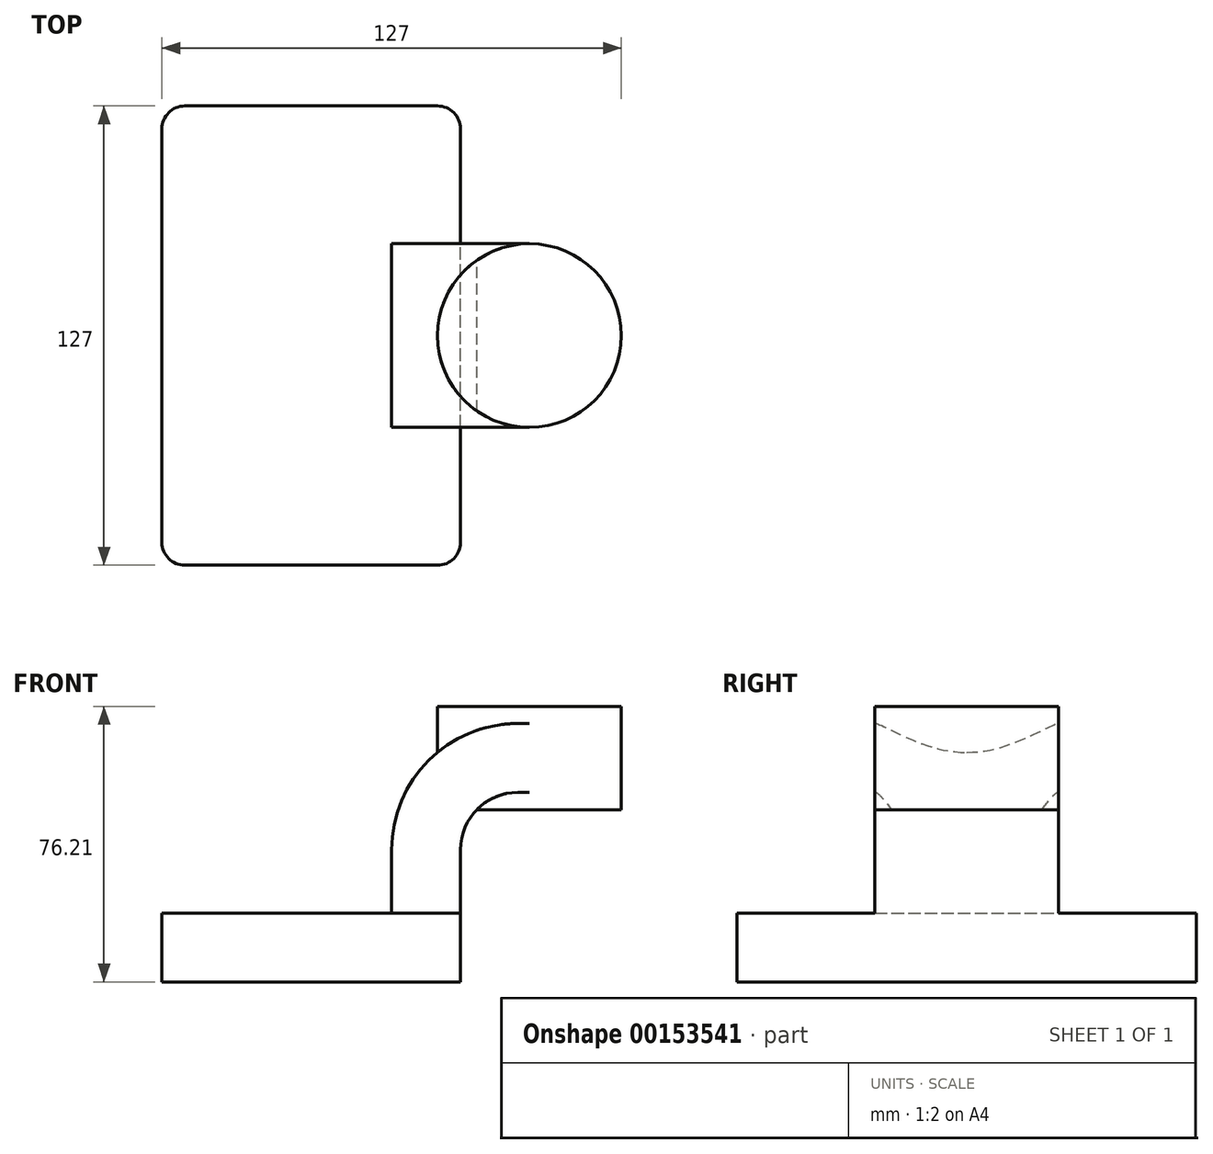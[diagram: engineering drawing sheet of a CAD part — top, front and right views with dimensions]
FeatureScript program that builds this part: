
annotation { "Feature Type Name" : "Feature", "Feature Type Description" : "" }
export const myFeature = defineFeature(function(context is Context, id is Id, definition is map)
    precondition{}
    {
        {
            var Q0;
            Q0=qCreatedBy(makeId("Front.planeOp"),FACE);
            var sketch = newSketch(context, id + "F0", { "sketchPlane" : qUnion([Q0])});
            skLineSegment(sketch, "E0.bottom", {"start": v(41.28, -9.52) * mm, "end": v(-41.27, -9.53) * mm});
            skLineSegment(sketch, "E0.top", {"start": v(41.27, 9.53) * mm, "end": v(-41.28, 9.53) * mm});
            skLineSegment(sketch, "E0.left", {"start": v(41.28, -9.52) * mm, "end": v(41.28, 9.53) * mm});
            skLineSegment(sketch, "E0.right", {"start": v(-41.27, -9.53) * mm, "end": v(-41.28, 9.53) * mm});
            skPoint(sketch, "E0.middle", {"position": v(0, 0) * mm});
            skLineSegment(sketch, "E1.bottom", {"start": v(111.12, 38.1) * mm, "end": v(60.33, 38.1) * mm});
            skLineSegment(sketch, "E1.top", {"start": v(111.12, 66.68) * mm, "end": v(60.33, 66.68) * mm});
            skLineSegment(sketch, "E1.left", {"start": v(111.12, 38.1) * mm, "end": v(111.12, 66.68) * mm});
            skLineSegment(sketch, "E1.right", {"start": v(60.33, 38.1) * mm, "end": v(60.33, 66.68) * mm});
            skPoint(sketch, "E1.middle", {"position": v(85.72, 52.39) * mm});
            skLineSegment(sketch, "E2", {"start": v(41.27, 9.53) * mm, "end": v(41.27, 27) * mm});
            skArc(sketch, "E3", {"start": v(41.27, 27) * mm, "mid": v(45.92, 38.23) * mm, "end": v(57.15, 42.88) * mm});
            skLineSegment(sketch, "E4", {"start": v(57.15, 42.88) * mm, "end": v(85.75, 42.88) * mm});
            skLineSegment(sketch, "E5.0", {"start": v(57.15, 61.93) * mm, "end": v(85.75, 61.93) * mm});
            skArc(sketch, "E5.1", {"start": v(22.23, 27) * mm, "mid": v(32.45, 51.7) * mm, "end": v(57.15, 61.93) * mm});
            skLineSegment(sketch, "E5.2", {"start": v(22.23, 9.53) * mm, "end": v(22.23, 27) * mm});
            skLineSegment(sketch, "E6", {"start": v(85.72, 38.1) * mm, "end": v(85.72, 66.68) * mm});
            skFitSpline(sketch, "E7", {"points": [v(-41.28, 9.53) * mm, v(57.15, 61.93) * mm], "startDerivative": vector(40.93, 87.18) * mm, "endDerivative": vector(191, -1.05) * mm});
            skSolve(sketch);
        }
        {
            var Q0;
            Q0=makeQuery(id+"F0.imprint","IMPRINT",FACE,{"disambiguationData":[TD([[makeQuery(id+"F0.imprint","IMPRINT",EDGE,{"derivedFrom":sQuery(id+"F0.wireOp",EDGE,"E0.bottom")}),-1.0]])]});
            extrude(context, id + "F1", {"entities" : qUnion([Q0]), "endBound" : BoundingType.SYMMETRIC, "depth" : 127 * mm});
        }
        {
            var Q0;
            {var subQ1=sQuery(id+"F0.wireOp",EDGE,"E2");Q0=makeQuery(id+"F0.imprint","IMPRINT",FACE,{"disambiguationData":[TD([[makeQuery(id+"F0.imprint","IMPRINT",EDGE,{"derivedFrom":subQ1}),1.0]])]});}
            extrude(context, id + "F2", {"entities" : qUnion([Q0]), "operationType" : NewBodyOperationType.ADD, "endBound" : BoundingType.SYMMETRIC, "depth" : 50.8 * mm});
        }
        {
            var Q0;
            Q0=makeQuery(id+"F0.imprint","IMPRINT",FACE,{"disambiguationData":[TD([[makeQuery(id+"F0.imprint","IMPRINT",EDGE,{"derivedFrom":sQuery(id+"F0.wireOp",EDGE,"E5.1")}),1.0]])]});
            extrude(context, id + "F3", {"entities" : qUnion([Q0]), "operationType" : NewBodyOperationType.ADD, "endBound" : BoundingType.SYMMETRIC, "depth" : 15.88 * mm});
        }
        {
            var Q0;
            {var subQ0=sQuery(id+"F0.wireOp",EDGE,"E1.right");var subQ1=sQuery(id+"F0.wireOp",EDGE,"E1.top");var subQ2=makeQuery(id+"F0.imprint","INTERSECT",VERTEX,{"derivedFrom":[subQ1,subQ0]});Q0=makeQuery(id+"F0.imprint","IMPRINT",FACE,{"disambiguationData":[TD([[makeQuery(id+"F0.imprint","IMPRINT",EDGE,{"disambiguationData":[TD([[subQ2,1.0]])],"derivedFrom":subQ1}),1.0]])]});}
            var Q1;
            {var subQ0=sQuery(id+"F0.wireOp",EDGE,"E1.right");var subQ1=sQuery(id+"F0.wireOp",EDGE,"E1.bottom");var subQ2=makeQuery(id+"F0.imprint","INTERSECT",VERTEX,{"derivedFrom":[subQ1,subQ0]});Q1=makeQuery(id+"F0.imprint","IMPRINT",FACE,{"disambiguationData":[TD([[makeQuery(id+"F0.imprint","IMPRINT",EDGE,{"disambiguationData":[TD([[subQ2,1.0]])],"derivedFrom":subQ1}),-1.0]])]});}
            var Q2;
            {var subQ0=sQuery(id+"F0.wireOp",EDGE,"E4");var subQ1=sQuery(id+"F0.wireOp",EDGE,"E1.right");var subQ2=makeQuery(id+"F0.imprint","INTERSECT",VERTEX,{"derivedFrom":[subQ1,subQ0]});Q2=makeQuery(id+"F0.imprint","IMPRINT",FACE,{"disambiguationData":[TD([[makeQuery(id+"F0.imprint","IMPRINT",EDGE,{"disambiguationData":[TD([[subQ2,-1.0]])],"derivedFrom":subQ1}),-1.0]])]});}
            var Q3;
            Q3=sQuery(id+"F0.wireOp",EDGE,"E1.right");
            revolve(context, id + "F4", {"operationType" : NewBodyOperationType.ADD, "entities" : qUnion([Q0, Q1, Q2]), "axis" : qUnion([Q3]), "revolveType" : RevolveType.FULL});
        }
        {
            var Q0;
            Q0=makeQuery(id+"F1.opExtrude","CAP_EDGE",EDGE,{"disambiguationData":[OSD([sQuery(id+"F0.wireOp",EDGE,"E0.left")])],"isStart":false});
            var Q1;
            Q1=makeQuery(id+"F1.opExtrude","CAP_EDGE",EDGE,{"disambiguationData":[OSD([sQuery(id+"F0.wireOp",EDGE,"E0.right")])],"isStart":false});
            var Q2;
            Q2=makeQuery(id+"F1.opExtrude","CAP_EDGE",EDGE,{"disambiguationData":[OSD([sQuery(id+"F0.wireOp",EDGE,"E0.left")])],"isStart":true});
            var Q3;
            Q3=makeQuery(id+"F1.opExtrude","CAP_EDGE",EDGE,{"disambiguationData":[OSD([sQuery(id+"F0.wireOp",EDGE,"E0.right")])],"isStart":true});
            fillet(context, id + "F5", {"entities" : qUnion([Q0, Q1, Q2, Q3]), "radius" : 6.35 * mm, "tangentPropagation" : true, "allowEdgeOverflow" : false});
        }
    });
